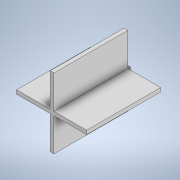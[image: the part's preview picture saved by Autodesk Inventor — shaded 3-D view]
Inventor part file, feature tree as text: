
AUTODESK INVENTOR PART (.ipt)
format: ipt  version: 2020 (Build 240168000, 168)  size: 117,248 bytes
history: native  units: mm
features: extrude x2, sketch x2
ambient origin geometry x8: Origin, YZ Plane, XZ Plane, XY Plane, X Axis, Y Axis, Z Axis, Center Point
bodies: Volumenkörper1 (feature_tree)
feature tree (4):
  extrude  "Extrusion1"  Depth=180.0mm
  extrude  "Extrusion2"  Depth=10.0mm
  sketch  "Skizze1"  dims[d0=10.0mm d1=180.0mm]
  sketch  "Skizze2"  dims[d2=90.0mm d3=10.0mm d4=180.0mm d5=90.0mm d6=190.0mm d7=0.0mm d8=7.0mm d9=0.0mm]
